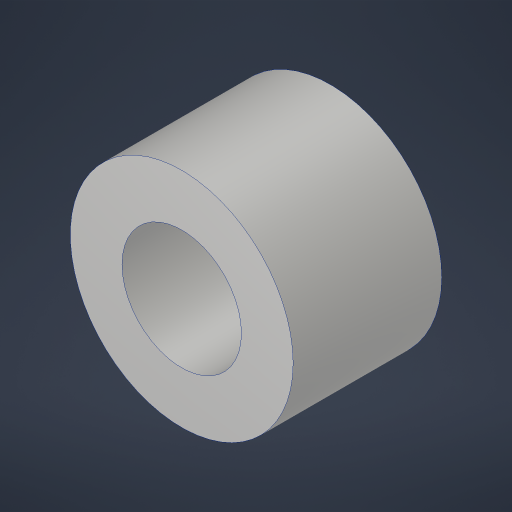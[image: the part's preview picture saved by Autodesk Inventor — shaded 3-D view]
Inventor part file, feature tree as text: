
AUTODESK INVENTOR PART (.ipt)
format: ipt  version: 2023.4 (Build 274418000, 418)  size: 174,080 bytes
history: native  units: in
note: dims shown in document units (in); Inventor stores cm internally (conversion verified against a paired STEP export)
features: extrude x1, hole x1
ambient origin geometry x8: Origin, YZ Plane, XZ Plane, XY Plane, X Axis, Y Axis, Z Axis, Center Point
bodies: Solid1 (feature_tree)
feature tree (2):
  extrude  "Extrusion1"  Depth=0.25in
  hole  "Hole1"  [1 undecoded]
note: 1 required parameter value undecoded (feature->parameter linkage not recoverable at this tier; creation-order binding heuristic only, values carry confidence <= 0.55)
